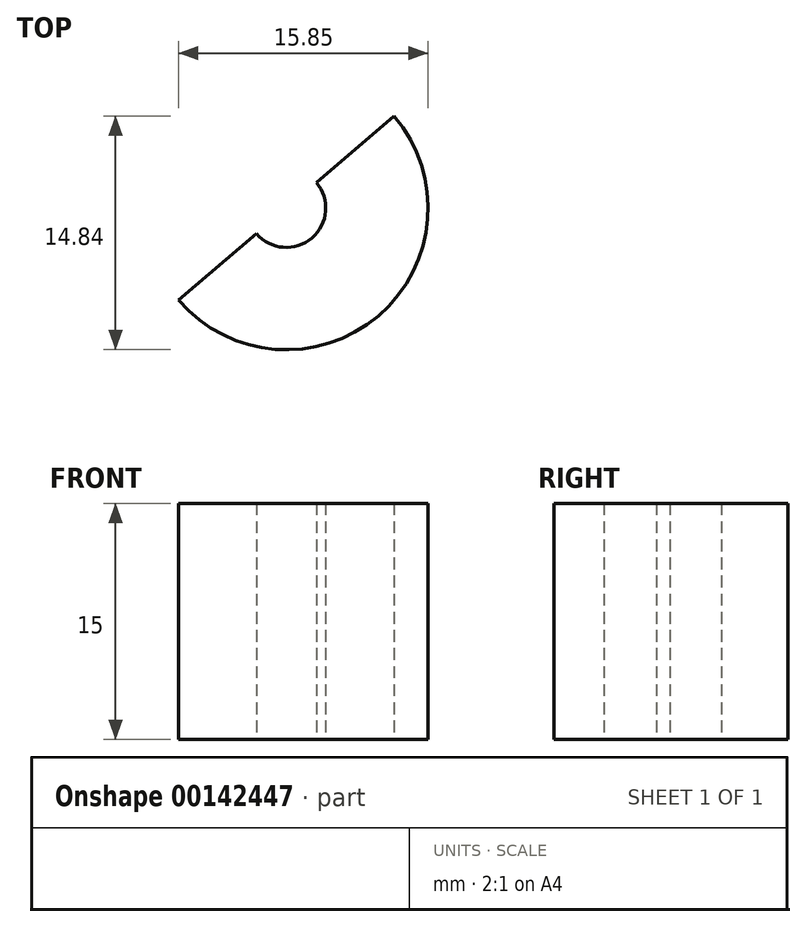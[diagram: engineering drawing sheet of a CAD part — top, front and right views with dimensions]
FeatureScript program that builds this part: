
annotation { "Feature Type Name" : "Feature", "Feature Type Description" : "" }
export const myFeature = defineFeature(function(context is Context, id is Id, definition is map)
    precondition{}
    {
        {
            var Q0;
            Q0=qCreatedBy(makeId("Top.planeOp"),FACE);
            var sketch = newSketch(context, id + "F0", { "sketchPlane" : qUnion([Q0])});
            skCircle(sketch, "E0", {"center": v(0, 0) * mm, "radius": 9 * mm});
            skCircle(sketch, "E1", {"center": v(0, 0) * mm, "radius": 2.5 * mm});
            skLineSegment(sketch, "E2", {"start": v(-6.85, -5.84) * mm, "end": v(0, 0) * mm});
            skLineSegment(sketch, "E3", {"start": v(0, 0) * mm, "end": v(6.85, 5.84) * mm});
            skSolve(sketch);
        }
        {
            var Q0;
            {var subQ0=sQuery(id+"F0.wireOp",EDGE,"E2");var subQ1=sQuery(id+"F0.wireOp",EDGE,"E0");var subQ2=makeQuery(id+"F0.imprint","INTERSECT",VERTEX,{"derivedFrom":[subQ1,subQ0]});Q0=makeQuery(id+"F0.imprint","IMPRINT",FACE,{"disambiguationData":[TD([[makeQuery(id+"F0.imprint","IMPRINT",EDGE,{"disambiguationData":[TD([[subQ2,-1.0]])],"derivedFrom":subQ1}),1.0]])]});}
            extrude(context, id + "F1", {"entities" : qUnion([Q0]), "depth" : 15 * mm});
        }
    });
